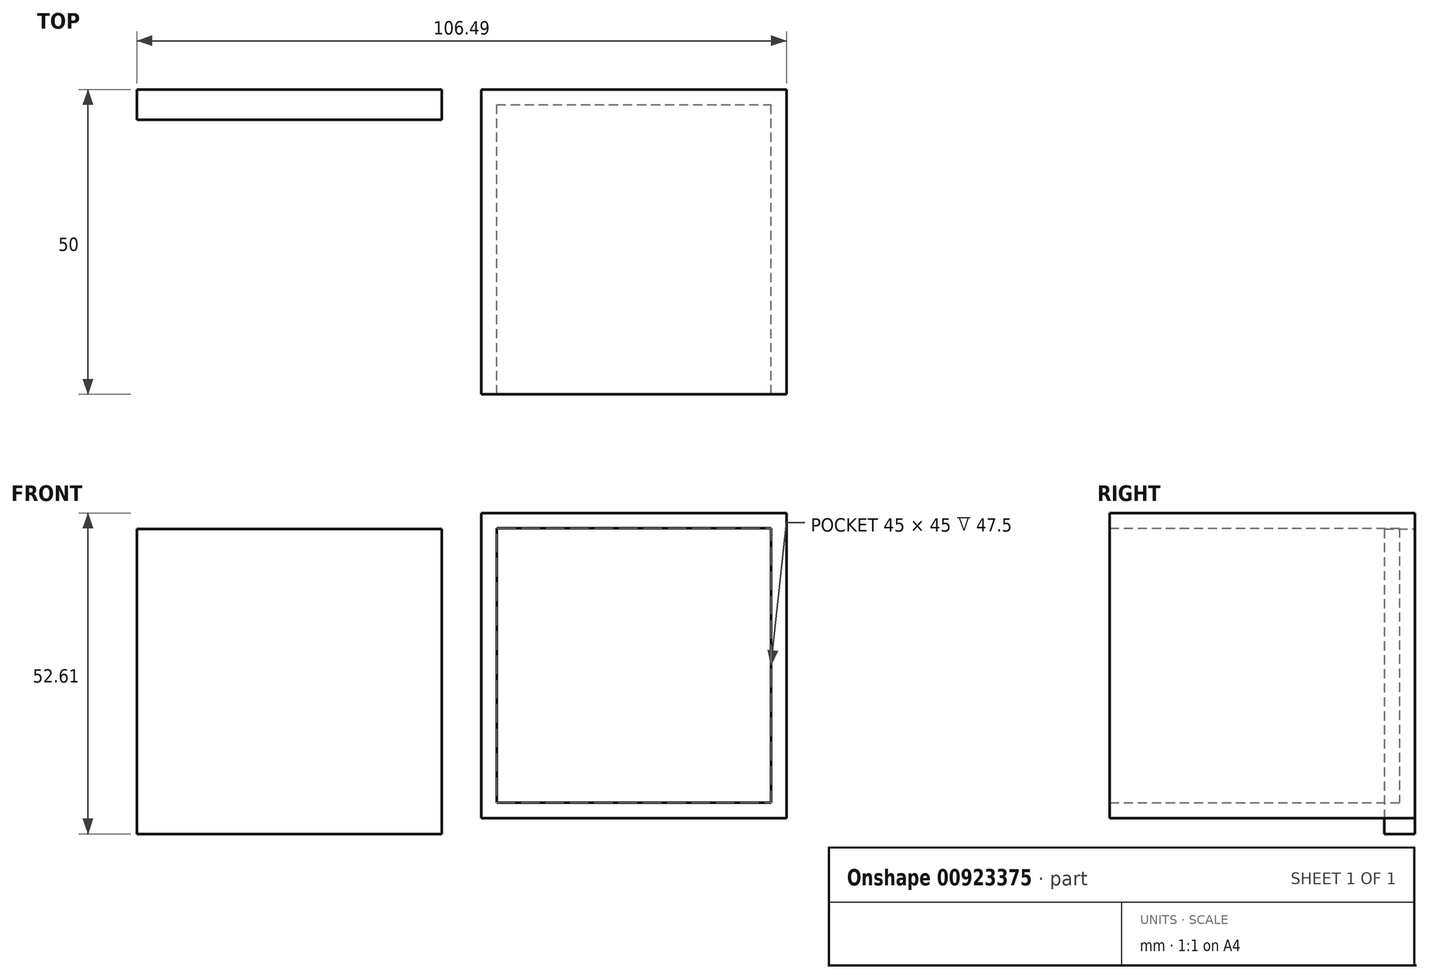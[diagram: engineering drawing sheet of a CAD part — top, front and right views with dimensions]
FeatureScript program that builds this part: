
annotation { "Feature Type Name" : "Feature", "Feature Type Description" : "" }
export const myFeature = defineFeature(function(context is Context, id is Id, definition is map)
    precondition{}
    {
        {
            var Q0;
            Q0=qCreatedBy(makeId("Front.planeOp"),FACE);
            var sketch = newSketch(context, id + "F0", { "sketchPlane" : qUnion([Q0])});
            skLineSegment(sketch, "E0.bottom", {"start": v(0, 0) * mm, "end": v(50, 0) * mm});
            skLineSegment(sketch, "E0.top", {"start": v(0, -50) * mm, "end": v(50, -50) * mm});
            skLineSegment(sketch, "E0.left", {"start": v(0, 0) * mm, "end": v(0, -50) * mm});
            skLineSegment(sketch, "E0.right", {"start": v(50, 0) * mm, "end": v(50, -50) * mm});
            skSolve(sketch);
        }
        {
            var Q0;
            Q0=makeQuery(id+"F0.imprint","IMPRINT",FACE,{"disambiguationData":[TD([[makeQuery(id+"F0.imprint","IMPRINT",EDGE,{"derivedFrom":sQuery(id+"F0.wireOp",EDGE,"E0.bottom")}),-1.0]])]});
            extrude(context, id + "F1", {"entities" : qUnion([Q0]), "depth" : 50 * mm, "offsetDistance" : 25 * mm});
        }
        {
            var Q0;
            Q0 = qSketchRegion(id + "F0", true);
            extrude(context, id + "F2", {"entities" : qUnion([Q0]), "operationType" : NewBodyOperationType.ADD, "depth" : 50 * mm, "offsetDistance" : 25 * mm});
        }
        {
            var Q0;
            Q0=makeQuery(id+"F1.opExtrude","CAP_FACE",FACE,{"disambiguationData":[OSD([sQuery(id+"F0.wireOp",EDGE,"E0.bottom"),sQuery(id+"F0.wireOp",EDGE,"E0.top"),sQuery(id+"F0.wireOp",EDGE,"E0.left"),sQuery(id+"F0.wireOp",EDGE,"E0.right")])],"isStart":false});
            shell(context, id + "F3", {"entities" : qUnion([Q0]), "thickness" : 2.5 * mm});
        }
        {
            var Q0;
            Q0=qCreatedBy(makeId("Front.planeOp"),FACE);
            var sketch = newSketch(context, id + "F4", { "sketchPlane" : qUnion([Q0])});
            skLineSegment(sketch, "E1.bottom", {"start": v(-56.49, -2.6) * mm, "end": v(-6.49, -2.6) * mm});
            skLineSegment(sketch, "E1.top", {"start": v(-56.49, -52.6) * mm, "end": v(-6.49, -52.6) * mm});
            skLineSegment(sketch, "E1.left", {"start": v(-56.49, -2.6) * mm, "end": v(-56.49, -52.6) * mm});
            skLineSegment(sketch, "E1.right", {"start": v(-6.49, -2.6) * mm, "end": v(-6.49, -52.6) * mm});
            skSolve(sketch);
        }
        {
            var Q0;
            Q0=makeQuery(id+"F4.imprint","IMPRINT",FACE,{"disambiguationData":[TD([[makeQuery(id+"F4.imprint","IMPRINT",EDGE,{"derivedFrom":sQuery(id+"F4.wireOp",EDGE,"E1.bottom")}),-1.0]])]});
            extrude(context, id + "F5", {"entities" : qUnion([Q0]), "depth" : 5 * mm, "offsetDistance" : 25 * mm});
        }
    });
